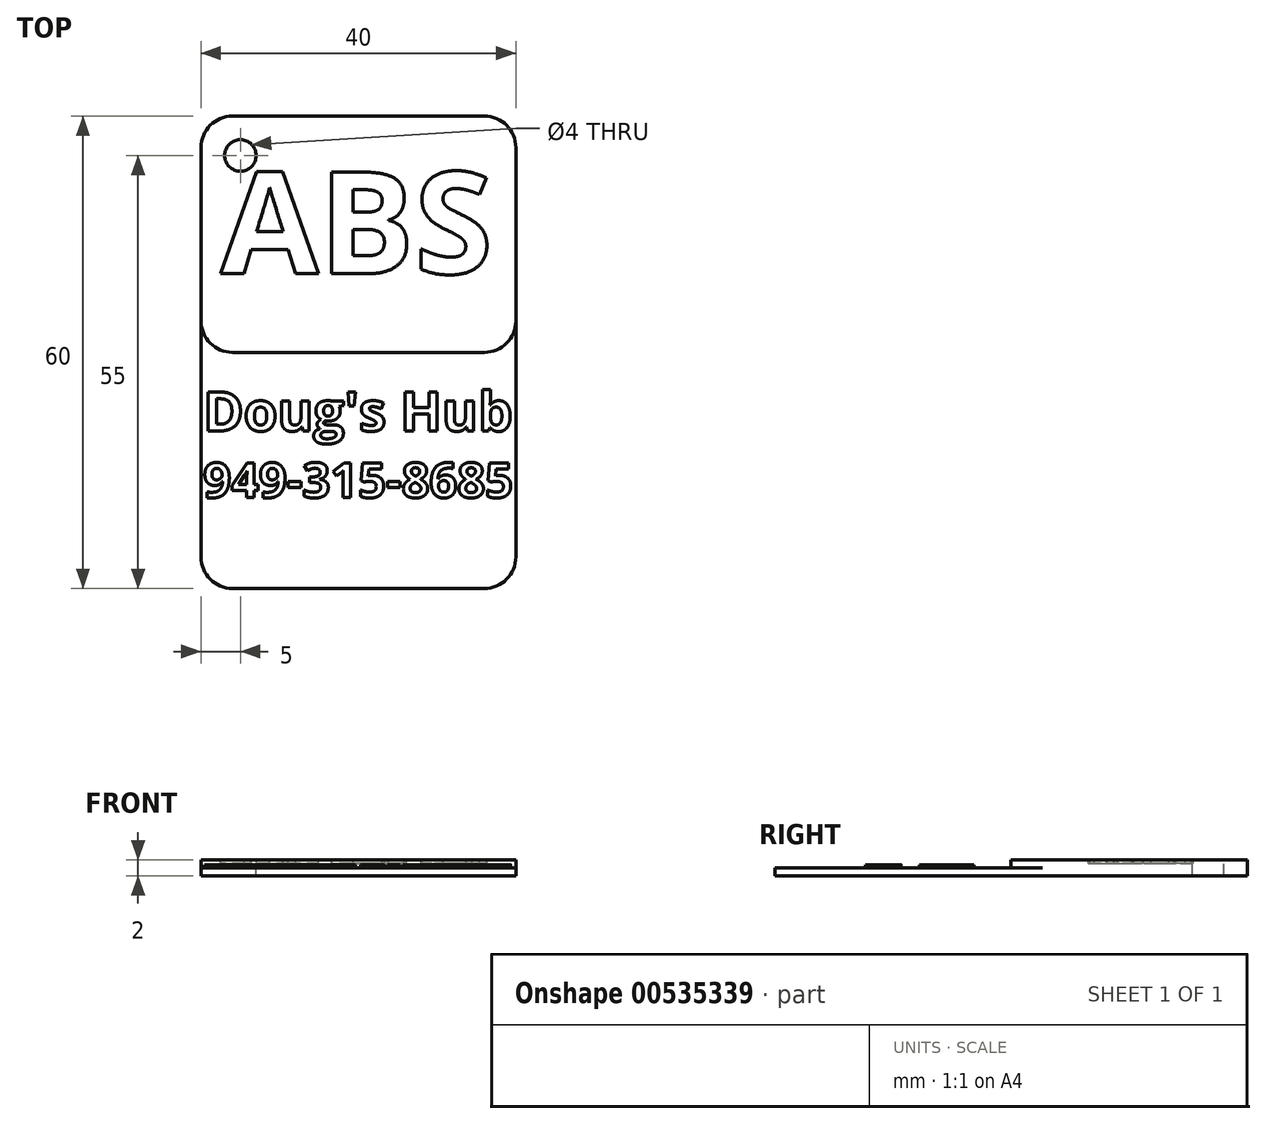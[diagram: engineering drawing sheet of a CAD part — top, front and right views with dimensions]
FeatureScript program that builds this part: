
annotation { "Feature Type Name" : "Feature", "Feature Type Description" : "" }
export const myFeature = defineFeature(function(context is Context, id is Id, definition is map)
    precondition{}
    {
        {
            var Q0;
            Q0=qCreatedBy(makeId("Top.planeOp"),FACE);
            var sketch = newSketch(context, id + "F0", { "sketchPlane" : qUnion([Q0])});
            skLineSegment(sketch, "E0.bottom", {"start": v(0, 0) * mm, "end": v(40, 0) * mm});
            skLineSegment(sketch, "E0.top", {"start": v(0, 60) * mm, "end": v(40, 60) * mm});
            skLineSegment(sketch, "E0.left", {"start": v(0, 0) * mm, "end": v(0, 60) * mm});
            skLineSegment(sketch, "E0.right", {"start": v(40, 0) * mm, "end": v(40, 60) * mm});
            skSolve(sketch);
        }
        {
            var Q0;
            Q0=qSketchRegion(id+"F0",true);
            extrude(context, id + "F1", {"entities" : qUnion([Q0]), "depth" : 1 * mm});
        }
        {
            var Q0;
            Q0=makeQuery(id+"F1.opExtrude","CAP_FACE",FACE,{"disambiguationData":[OSD([sQuery(id+"F0.wireOp",EDGE,"E0.bottom"),sQuery(id+"F0.wireOp",EDGE,"E0.top"),sQuery(id+"F0.wireOp",EDGE,"E0.left"),sQuery(id+"F0.wireOp",EDGE,"E0.right")])],"isStart":false});
            var sketch = newSketch(context, id + "F2", { "sketchPlane" : qUnion([Q0])});
            skLineSegment(sketch, "E1.bottom", {"start": v(0, 60) * mm, "end": v(40, 60) * mm});
            skLineSegment(sketch, "E1.top", {"start": v(0, 30) * mm, "end": v(40, 30) * mm});
            skLineSegment(sketch, "E1.left", {"start": v(0, 60) * mm, "end": v(0, 30) * mm});
            skLineSegment(sketch, "E1.right", {"start": v(40, 60) * mm, "end": v(40, 30) * mm});
            skSolve(sketch);
        }
        {
            var Q0;
            Q0=qSketchRegion(id+"F2",true);
            extrude(context, id + "F3", {"entities" : qUnion([Q0]), "operationType" : NewBodyOperationType.ADD, "depth" : 1 * mm});
        }
        {
            var Q0;
            Q0=makeQuery(id+"F1.opExtrude","CAP_FACE",FACE,{"disambiguationData":[OSD([sQuery(id+"F0.wireOp",EDGE,"E0.bottom"),sQuery(id+"F0.wireOp",EDGE,"E0.top"),sQuery(id+"F0.wireOp",EDGE,"E0.left"),sQuery(id+"F0.wireOp",EDGE,"E0.right")])],"isStart":false});
            var sketch = newSketch(context, id + "F4", { "sketchPlane" : qUnion([Q0])});
            skPoint(sketch, "E2.oppositeSnap0", {"position": v(20, 25) * mm});
            skLineSegment(sketch, "E2.bottom", {"start": v(24.97, 0) * mm, "end": v(24.97, 0) * mm});
            skText(sketch, "E3", { "text": "Doug\'s Hub", "fontName": "OpenSans-Bold.ttf"});
            skText(sketch, "E4", { "text": "949-315-8685", "fontName": "OpenSans-Bold.ttf"});
            const initialGuessF4  = {"E3": [0.00028, 0.02, 1, 0, 0.005], "E4": [0.00028, 0.01154, 1, 0, 0.00446]};
            skSetInitialGuess(sketch, initialGuessF4);
            skSolve(sketch);
        }
        {
            var Q0;
            Q0=qSketchRegion(id+"F4",true);
            extrude(context, id + "F5", {"entities" : qUnion([Q0]), "operationType" : NewBodyOperationType.ADD, "depth" : .4 * mm});
        }
        {
            var Q0;
            Q0=makeQuery(id+"F3.opExtrude","CAP_FACE",FACE,{"disambiguationData":[OSD([sQuery(id+"F2.wireOp",EDGE,"E1.bottom"),sQuery(id+"F2.wireOp",EDGE,"E1.top"),sQuery(id+"F2.wireOp",EDGE,"E1.left"),sQuery(id+"F2.wireOp",EDGE,"E1.right")])],"isStart":false});
            var sketch = newSketch(context, id + "F6", { "sketchPlane" : qUnion([Q0])});
            skText(sketch, "E5", { "text": "ABS", "fontName": "OpenSans-Bold.ttf"});
            const initialGuessF6  = {"E5": [0.0025, 0.04, 1, 0, 0.013]};
            skSetInitialGuess(sketch, initialGuessF6);
            skSolve(sketch);
        }
        {
            var Q0;
            Q0=qSketchRegion(id+"F6",true);
            extrude(context, id + "F7", {"entities" : qUnion([Q0]), "operationType" : NewBodyOperationType.REMOVE, "oppositeDirection" : true, "depth" : .4 * mm});
        }
        {
            var Q0;
            {var subQ0=sQuery(id+"F2.wireOp",EDGE,"E1.left");var subQ1=sQuery(id+"F2.wireOp",EDGE,"E1.top");var subQ2=sQuery(id+"F2.wireOp",EDGE,"E1.bottom");var subQ3=sQuery(id+"F2.wireOp",EDGE,"E1.right");Q0=makeQuery(id+"F7.boolean.opBoolean","SPLIT",FACE,{"disambiguationData":[TD([makeQuery(id+"F1.opExtrude","SWEPT_FACE",FACE,{"disambiguationData":[OSD([sQuery(id+"F0.wireOp",EDGE,"E0.top")])]})])],"derivedFrom":makeQuery(id+"F3.opExtrude","CAP_FACE",FACE,{"disambiguationData":[OSD([subQ2,subQ1,subQ0,subQ3])],"isStart":false})});}
            var sketch = newSketch(context, id + "F8", { "sketchPlane" : qUnion([Q0])});
            skCircle(sketch, "E6", {"center": v(5, 55) * mm, "radius": 2 * mm});
            skSolve(sketch);
        }
        {
            var Q0;
            Q0=qSketchRegion(id+"F8",true);
            extrude(context, id + "F9", {"entities" : qUnion([Q0]), "operationType" : NewBodyOperationType.REMOVE, "endBound" : BoundingType.THROUGH_ALL, "oppositeDirection" : true, "depth" : 25.4 * mm});
        }
        {
            var Q0;
            Q0=makeQuery(id+"F3.opExtrude","SWEPT_EDGE",EDGE,{"disambiguationData":[OSD([sQuery(id+"F0.wireOp",EDGE,"E0.left"),sQuery(id+"F2.wireOp",EDGE,"E1.top"),sQuery(id+"F2.wireOp",EDGE,"E1.left")])]});
            var Q1;
            Q1=makeQuery(id+"F3.opExtrude","SWEPT_EDGE",EDGE,{"disambiguationData":[OSD([sQuery(id+"F0.wireOp",EDGE,"E0.right"),sQuery(id+"F2.wireOp",EDGE,"E1.top"),sQuery(id+"F2.wireOp",EDGE,"E1.right")])]});
            var Q2;
            Q2=makeQuery(id+"F1.opExtrude","SWEPT_EDGE",EDGE,{"disambiguationData":[OSD([sQuery(id+"F0.wireOp",EDGE,"E0.bottom"),sQuery(id+"F0.wireOp",EDGE,"E0.left")])]});
            var Q3;
            Q3=makeQuery(id+"F1.opExtrude","SWEPT_EDGE",EDGE,{"disambiguationData":[OSD([sQuery(id+"F0.wireOp",EDGE,"E0.bottom"),sQuery(id+"F0.wireOp",EDGE,"E0.right")])]});
            var Q4;
            Q4=makeQuery(id+"F3.boolean.opBoolean","MERGE",EDGE,{"derivedFrom":[makeQuery(id+"F1.opExtrude","SWEPT_EDGE",EDGE,{"disambiguationData":[OSD([sQuery(id+"F0.wireOp",EDGE,"E0.top"),sQuery(id+"F0.wireOp",EDGE,"E0.right")])]}),makeQuery(id+"F3.opExtrude","SWEPT_EDGE",EDGE,{"disambiguationData":[OSD([sQuery(id+"F2.wireOp",EDGE,"E1.bottom"),sQuery(id+"F2.wireOp",EDGE,"E1.right")])]})]});
            var Q5;
            Q5=makeQuery(id+"F3.boolean.opBoolean","MERGE",EDGE,{"derivedFrom":[makeQuery(id+"F1.opExtrude","SWEPT_EDGE",EDGE,{"disambiguationData":[OSD([sQuery(id+"F0.wireOp",EDGE,"E0.top"),sQuery(id+"F0.wireOp",EDGE,"E0.left")])]}),makeQuery(id+"F3.opExtrude","SWEPT_EDGE",EDGE,{"disambiguationData":[OSD([sQuery(id+"F2.wireOp",EDGE,"E1.bottom"),sQuery(id+"F2.wireOp",EDGE,"E1.left")])]})]});
            fillet(context, id + "F10", {"entities" : qUnion([Q0, Q1, Q2, Q3, Q4, Q5]), "radius" : 4 * mm, "tangentPropagation" : true, "allowEdgeOverflow" : false});
        }
    });
